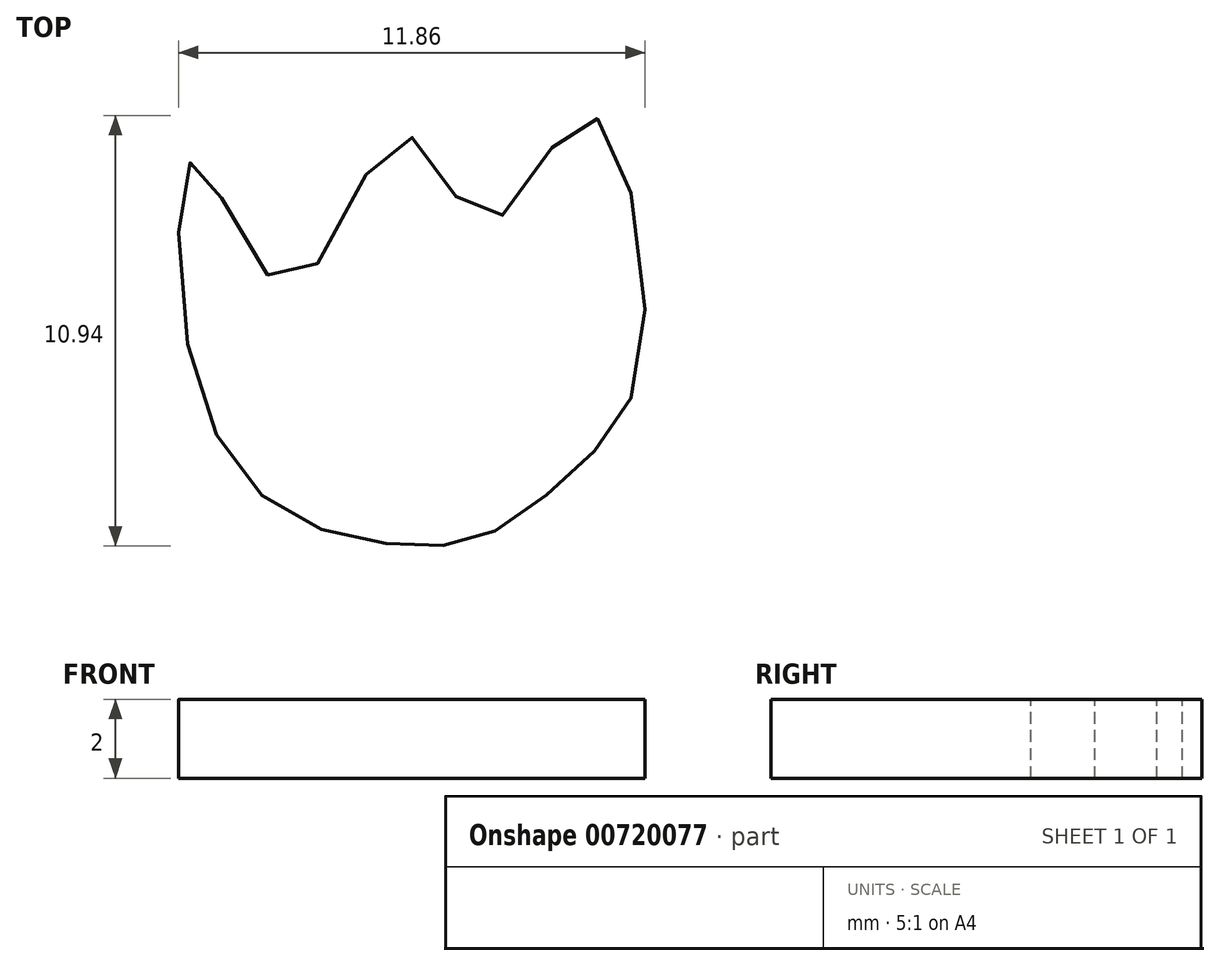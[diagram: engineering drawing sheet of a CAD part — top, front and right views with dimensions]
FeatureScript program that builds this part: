
annotation { "Feature Type Name" : "Feature", "Feature Type Description" : "" }
export const myFeature = defineFeature(function(context is Context, id is Id, definition is map)
    precondition{}
    {
        {
            var Q0;
            Q0=qCreatedBy(makeId("Top.planeOp"),FACE);
            var sketch = newSketch(context, id + "F0", { "sketchPlane" : qUnion([Q0])});
            skFitSpline(sketch, "E0", {"points": [v(-5.44, 0) * mm, v(-3.04, -4.23) * mm, v(0, -5.1) * mm, v(2.15, -4.85) * mm, v(4.5, -3.08) * mm, v(6.14, 0) * mm, v(4.65, 5.8) * mm, v(2.13, 3.1) * mm, v(0, 5.31) * mm, v(-2.86, 1.47) * mm, v(-5.2, 4.64) * mm, v(-5.44, 0) * mm]});
            skSolve(sketch);
        }
        {
            var Q0;
            Q0=sQuery(id+"F0.wireOp",EDGE,"E0");
            extrude(context, id + "F1", {"bodyType" : ToolBodyType.SURFACE, "surfaceEntities" : qUnion([Q0]), "depth" : 2 * mm, "offsetDistance" : 25.4 * mm});
        }
    });
